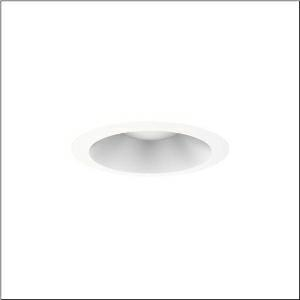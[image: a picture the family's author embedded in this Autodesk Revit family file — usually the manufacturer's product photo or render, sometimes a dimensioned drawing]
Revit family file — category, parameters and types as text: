
# Revit family: lunis_31_midi_51dn167g32
name_source: partatom
category: Lighting Fixtures
units: mm (PartAtom-declared; Revit-internal decimal feet)

## family parameters
Cut with Voids When Loaded = No
Host = Face
Light Source = No
Part Type = Normal
Room Calculation Point = No
Round Connector Dimension = Use Diameter
Shared = No

## types (1)
- Lunis 31 midi (1 x LED, 2000 lm, 17 W, 3000K)
    Apparent Load = 17 VA
    CIE Flux Codes = 64 93 99 100 100
    Color Rendering = 80
    Color Temperature = 3000K
    Default Elevation = 1800 mm
    Description = Lunis 31,  midi, downlight, light control with reflector, light emission: direct distribution, LED rated luminous flux: 2.050lm, light colour: 830, control gear: ECG, mains connection: 220..240V, AC, 50/60Hz, housing, white, protection rating (complete): IP20, insulation class (complete): insulation class II (safety insulation), certification: CE, packaging unit: 1 piece
    Height = 0 mm  [stored 0 ft]
    Lamp = 1 x LED
    Lamp Light Flux = 2000 lm
    Lamp Power = 17 W
    Lamp count = 1
    Length = 259 mm
    Luminous efficacy = 118 lm/W
    Manufacturer = Siteco
    ModVariant = No
    Model = 51DN167G32
    Mounting Place = Ceiling
    Mounting Type = Recessed
    Number of Poles = 1
    OnlyDefault = Yes
    Power Factor = 1
    Product Name = Lunis 31 midi
    Product group = downlight | ceiling recessed
    ProductGroupID = 402
    Protection Class = Protection class II
    Protection Degree = IP 20
    RLX_Detail_Level = 1
    RlxData = <blob elided: 23649 chars, md5=05486f17>
    Socket = socket
    Standby Power = 0 W
    System Light Flux = 2000 lm
    System Power = 17 W
    Type Comments = Product without accessories
    Type Image = l_1006711.jpg
    URL = http://relux.com
    VarID = ---
    Voltage = 0 V
    Weight = 0.00 kg
    Width = 0 mm  [stored 0 ft]

note: [stored X ft] marks values corroborated as IEEE doubles in the binary element streams (Revit-internal decimal feet)

## geometry (parser evidence)
native form markers: Blend x4, Sweep x12
no freeform markers — native parametric forms only
